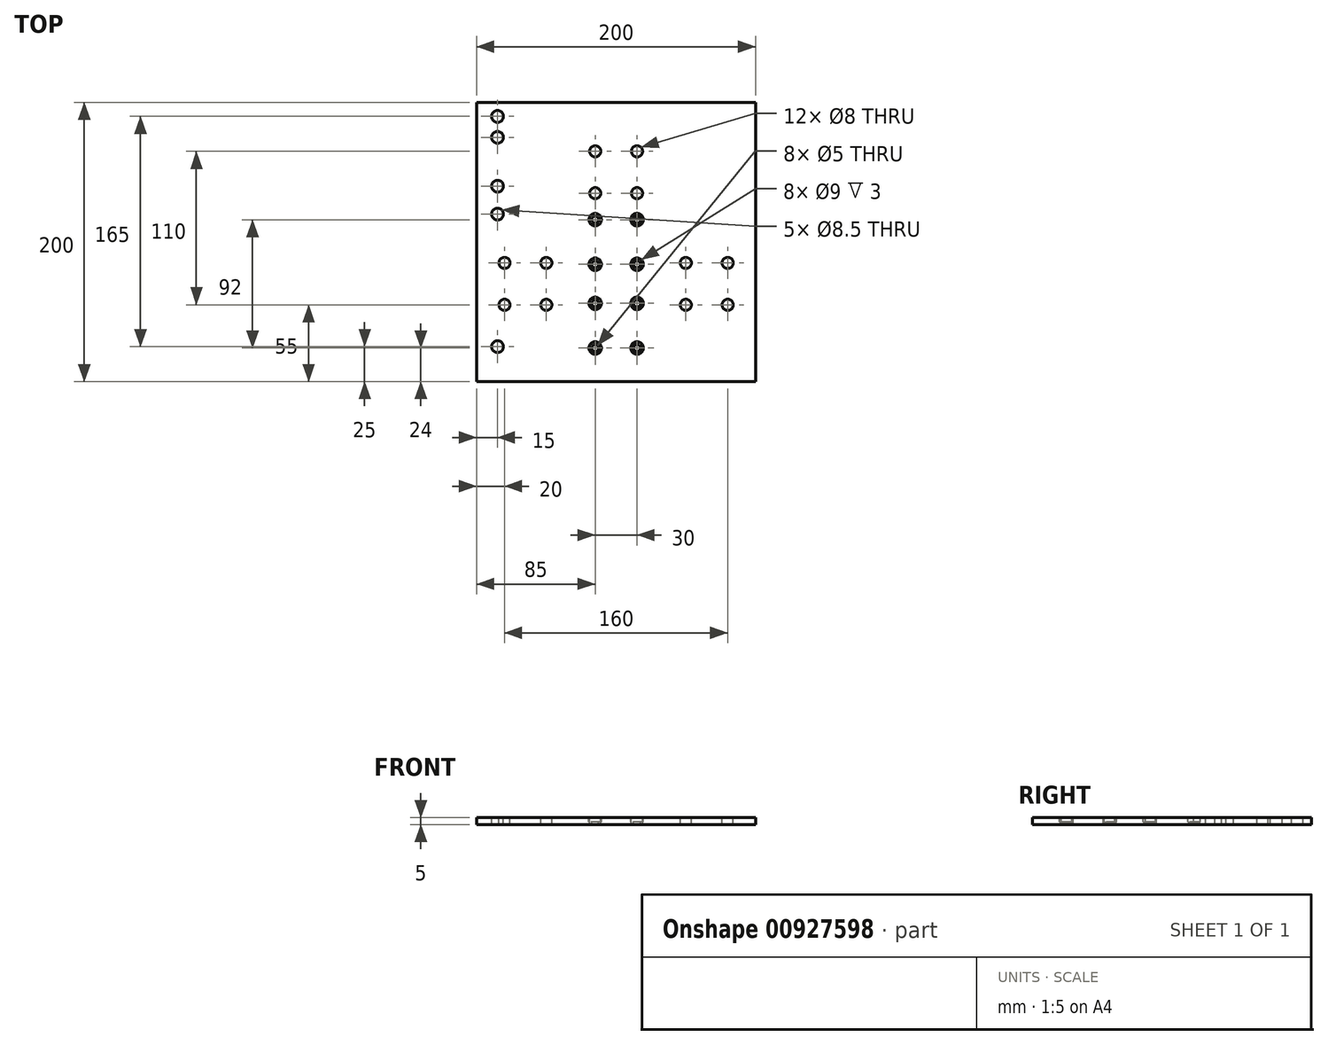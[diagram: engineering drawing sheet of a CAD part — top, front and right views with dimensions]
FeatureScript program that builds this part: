
annotation { "Feature Type Name" : "Feature", "Feature Type Description" : "" }
export const myFeature = defineFeature(function(context is Context, id is Id, definition is map)
    precondition{}
    {
        {
            var Q0;
            Q0=qCreatedBy(makeId("Right.planeOp"),FACE);
            var sketch = newSketch(context, id + "F0", { "sketchPlane" : qUnion([Q0])});
            skLineSegment(sketch, "E0.bottom", {"start": v(-200, 5) * mm, "end": v(0, 5) * mm});
            skLineSegment(sketch, "E0.top", {"start": v(-200, 0) * mm, "end": v(0, 0) * mm});
            skLineSegment(sketch, "E0.left", {"start": v(-200, 5) * mm, "end": v(-200, 0) * mm});
            skLineSegment(sketch, "E0.right", {"start": v(0, 5) * mm, "end": v(0, 0) * mm});
            skSolve(sketch);
        }
        {
            var Q0;
            Q0 = qSketchRegion(id + "F0", true);
            extrude(context, id + "F1", {"entities" : qUnion([Q0]), "oppositeDirection" : true, "depth" : 200 * mm, "offsetDistance" : 25 * mm});
        }
        {
            var Q0;
            Q0=makeQuery(id+"F1.opExtrude","SWEPT_FACE",FACE,{"disambiguationData":[OSD([sQuery(id+"F0.wireOp",EDGE,"E0.bottom")])]});
            var sketch = newSketch(context, id + "F2", { "sketchPlane" : qUnion([Q0])});
            skLineSegment(sketch, "E1", {"start": v(-225.72, -100) * mm, "end": v(35.36, -100) * mm, "construction": true});
            skPoint(sketch, "E1.startSnap0", {"position": v(-200, -100) * mm});
            skLineSegment(sketch, "E2", {"start": v(-100, 18.42) * mm, "end": v(-100, -202.55) * mm, "construction": true});
            skPoint(sketch, "E2.startSnap0", {"position": v(-100, 0) * mm});
            skCircle(sketch, "E3", {"center": v(-85, -84) * mm, "radius": 2.5 * mm});
            skCircle(sketch, "E4.MirrorC", {"center": v(-115, -84) * mm, "radius": 2.5 * mm});
            skCircle(sketch, "E5.MirrorC", {"center": v(-85, -116) * mm, "radius": 2.5 * mm});
            skCircle(sketch, "E6.MirrorC", {"center": v(-115, -116) * mm, "radius": 2.5 * mm});
            skLineSegment(sketch, "E7", {"start": v(-182.3, -160) * mm, "end": v(30.52, -160) * mm, "construction": true});
            skCircle(sketch, "E8", {"center": v(-85, -144) * mm, "radius": 2.5 * mm});
            skCircle(sketch, "E9.MirrorC", {"center": v(-115, -144) * mm, "radius": 2.5 * mm});
            skCircle(sketch, "E10.MirrorC", {"center": v(-85, -176) * mm, "radius": 2.5 * mm});
            skCircle(sketch, "E11.MirrorC", {"center": v(-115, -176) * mm, "radius": 2.5 * mm});
            skSolve(sketch);
        }
        {
            var Q0;
            Q0 = qSketchRegion(id + "F2", true);
            extrude(context, id + "F3", {"entities" : qUnion([Q0]), "operationType" : NewBodyOperationType.REMOVE, "endBound" : BoundingType.THROUGH_ALL, "oppositeDirection" : true, "depth" : 25 * mm, "offsetDistance" : 25 * mm});
        }
        {
            var Q0;
            Q0=makeQuery(id+"F1.opExtrude","SWEPT_FACE",FACE,{"disambiguationData":[OSD([sQuery(id+"F0.wireOp",EDGE,"E0.bottom")])]});
            var sketch = newSketch(context, id + "F4", { "sketchPlane" : qUnion([Q0])});
            skLineSegment(sketch, "E12", {"start": v(-185, 42.52) * mm, "end": v(-185, -212.47) * mm, "construction": true});
            skCircle(sketch, "E13", {"center": v(-185, -25) * mm, "radius": 4.25 * mm});
            skCircle(sketch, "E14", {"center": v(-185, -60) * mm, "radius": 4.25 * mm});
            skCircle(sketch, "E15", {"center": v(-185, -10) * mm, "radius": 4.25 * mm});
            skCircle(sketch, "E16", {"center": v(-185, -175) * mm, "radius": 4.25 * mm});
            skCircle(sketch, "E17", {"center": v(-185, -80) * mm, "radius": 4.25 * mm});
            skSolve(sketch);
        }
        {
            var Q0;
            Q0 = qSketchRegion(id + "F4", true);
            extrude(context, id + "F5", {"entities" : qUnion([Q0]), "operationType" : NewBodyOperationType.REMOVE, "endBound" : BoundingType.THROUGH_ALL, "oppositeDirection" : true, "depth" : 25 * mm, "offsetDistance" : 25 * mm});
        }
        {
            var Q0;
            Q0=makeQuery(id+"F1.opExtrude","SWEPT_FACE",FACE,{"disambiguationData":[OSD([sQuery(id+"F0.wireOp",EDGE,"E0.bottom")])]});
            var sketch = newSketch(context, id + "F6", { "sketchPlane" : qUnion([Q0])});
            skCircle(sketch, "E18", {"center": v(-115, -84) * mm, "radius": 4.5 * mm});
            skCircle(sketch, "E19", {"center": v(-85, -84) * mm, "radius": 4.5 * mm});
            skCircle(sketch, "E20", {"center": v(-115, -116) * mm, "radius": 4.5 * mm});
            skCircle(sketch, "E21", {"center": v(-85, -116) * mm, "radius": 4.5 * mm});
            skCircle(sketch, "E22", {"center": v(-115, -144) * mm, "radius": 4.5 * mm});
            skCircle(sketch, "E23", {"center": v(-85, -144) * mm, "radius": 4.5 * mm});
            skCircle(sketch, "E24", {"center": v(-115, -176) * mm, "radius": 4.5 * mm});
            skCircle(sketch, "E25", {"center": v(-85, -176) * mm, "radius": 4.5 * mm});
            skSolve(sketch);
        }
        {
            var Q0;
            Q0 = qSketchRegion(id + "F6", true);
            extrude(context, id + "F7", {"entities" : qUnion([Q0]), "operationType" : NewBodyOperationType.REMOVE, "oppositeDirection" : true, "depth" : 3 * mm, "offsetDistance" : 25 * mm});
        }
        {
            var Q0;
            Q0=makeQuery(id+"F1.opExtrude","SWEPT_FACE",FACE,{"disambiguationData":[OSD([sQuery(id+"F0.wireOp",EDGE,"E0.bottom")])]});
            var sketch = newSketch(context, id + "F8", { "sketchPlane" : qUnion([Q0])});
            skPoint(sketch, "E26.startSnap0", {"position": v(-100, 0) * mm});
            skPoint(sketch, "E27.startSnap0", {"position": v(-200, -100) * mm});
            skPoint(sketch, "E28", {"position": v(-100, -130) * mm});
            skLineSegment(sketch, "E29", {"start": v(-100, 18.07) * mm, "end": v(-100, -224.34) * mm, "construction": true});
            skLineSegment(sketch, "E30.bottom", {"start": v(-70, -160) * mm, "end": v(-130, -160) * mm, "construction": true});
            skLineSegment(sketch, "E30.top", {"start": v(-70, -100) * mm, "end": v(-130, -100) * mm, "construction": true});
            skLineSegment(sketch, "E30.left", {"start": v(-70, -160) * mm, "end": v(-70, -100) * mm, "construction": true});
            skLineSegment(sketch, "E30.right", {"start": v(-130, -160) * mm, "end": v(-130, -100) * mm, "construction": true});
            skLineSegment(sketch, "E31", {"start": v(-85, 16) * mm, "end": v(-85, -208.09) * mm, "construction": true});
            skLineSegment(sketch, "E32", {"start": v(-225.72, -145) * mm, "end": v(78.94, -145) * mm, "construction": true});
            skCircle(sketch, "E33", {"center": v(-150, -145) * mm, "radius": 4 * mm});
            skCircle(sketch, "E34", {"center": v(-180, -145) * mm, "radius": 4 * mm});
            skCircle(sketch, "E35.MirrorC", {"center": v(-20, -145) * mm, "radius": 4 * mm});
            skCircle(sketch, "E36.MirrorC", {"center": v(-50, -145) * mm, "radius": 4 * mm});
            skLineSegment(sketch, "E37", {"start": v(-211.1, -130) * mm, "end": v(-9.34, -130) * mm, "construction": true});
            skCircle(sketch, "E38.MirrorC", {"center": v(-20, -115) * mm, "radius": 4 * mm});
            skCircle(sketch, "E39.MirrorC", {"center": v(-50, -115) * mm, "radius": 4 * mm});
            skCircle(sketch, "E40.MirrorC", {"center": v(-150, -115) * mm, "radius": 4 * mm});
            skCircle(sketch, "E41.MirrorC", {"center": v(-180, -115) * mm, "radius": 4 * mm});
            skLineSegment(sketch, "E42", {"start": v(-169.07, -65) * mm, "end": v(3.66, -65) * mm, "construction": true});
            skCircle(sketch, "E43", {"center": v(-85, -65) * mm, "radius": 4 * mm});
            skCircle(sketch, "E44", {"center": v(-85, -35) * mm, "radius": 4 * mm});
            skCircle(sketch, "E45.MirrorC", {"center": v(-115, -35) * mm, "radius": 4 * mm});
            skCircle(sketch, "E46.MirrorC", {"center": v(-115, -65) * mm, "radius": 4 * mm});
            skSolve(sketch);
        }
        {
            var Q0;
            Q0 = qSketchRegion(id + "F8", true);
            extrude(context, id + "F9", {"entities" : qUnion([Q0]), "operationType" : NewBodyOperationType.REMOVE, "oppositeDirection" : true, "depth" : 25 * mm, "offsetDistance" : 25 * mm});
        }
    });
